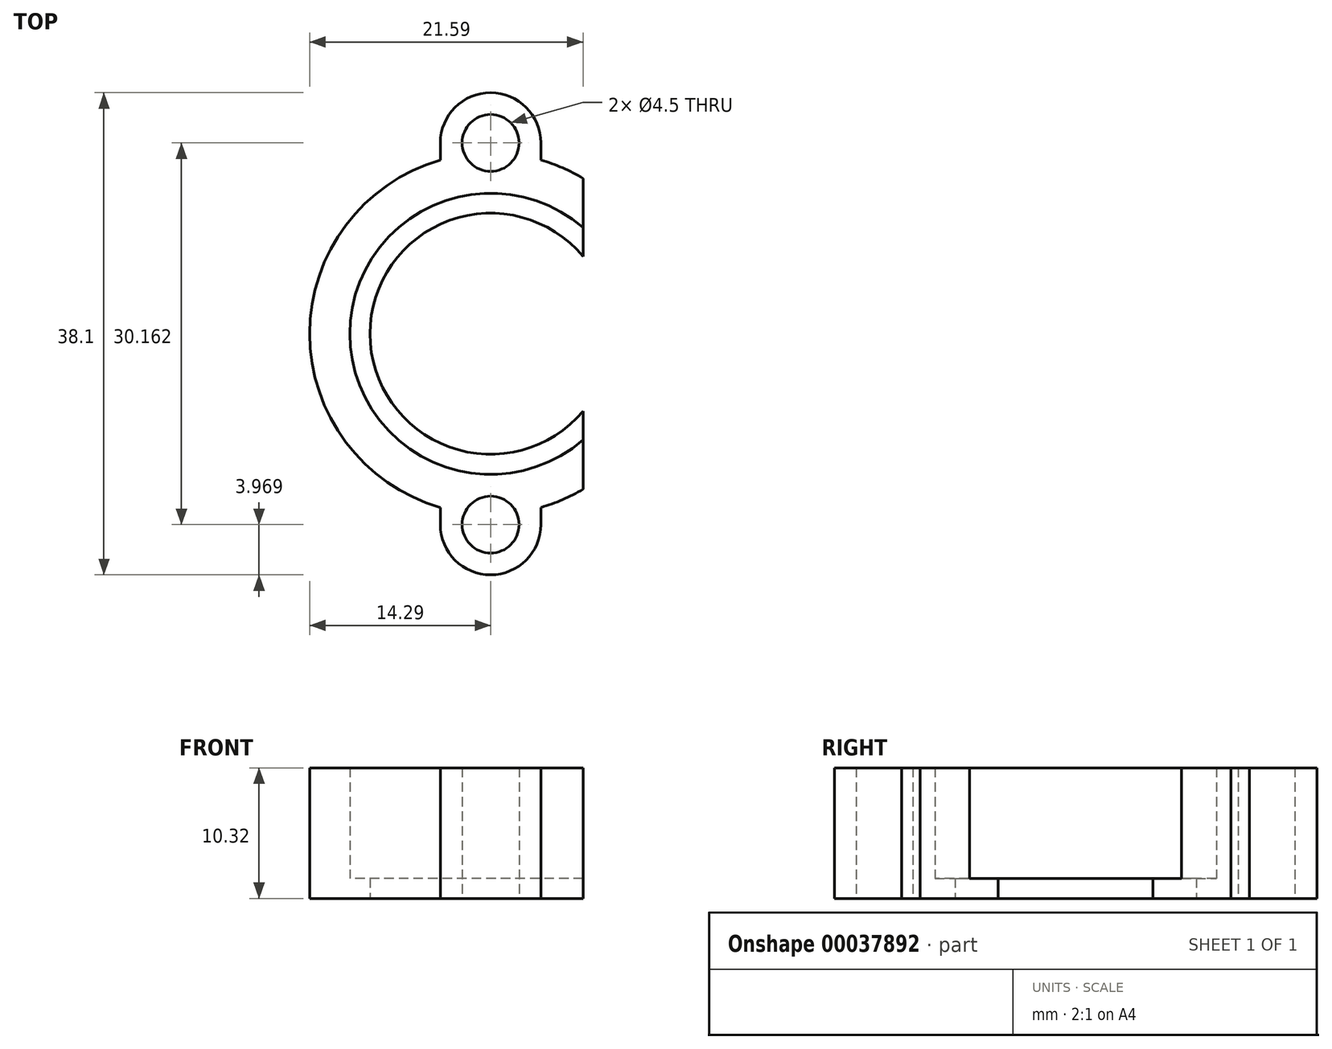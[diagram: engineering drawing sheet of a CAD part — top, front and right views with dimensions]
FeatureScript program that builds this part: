
annotation { "Feature Type Name" : "Feature", "Feature Type Description" : "" }
export const myFeature = defineFeature(function(context is Context, id is Id, definition is map)
    precondition{}
    {
        {
            var Q0;
            Q0=qCreatedBy(makeId("Top.planeOp"),FACE);
            var sketch = newSketch(context, id + "F0", { "sketchPlane" : qUnion([Q0])});
            skCircle(sketch, "E0", {"center": v(0, 0) * mm, "radius": 9.53 * mm});
            skArc(sketch, "E1", {"start": v(3.97, -13.73) * mm, "mid": v(14.29, 0) * mm, "end": v(3.97, 13.73) * mm});
            skArc(sketch, "E2", {"start": v(-3.97, 13.73) * mm, "mid": v(-14.29, 0) * mm, "end": v(-3.97, -13.73) * mm});
            skLineSegment(sketch, "E3", {"start": v(0, -15.08) * mm, "end": v(0, 15.08) * mm, "construction": true});
            skLineSegment(sketch, "E4", {"start": v(-3.97, 15.08) * mm, "end": v(3.97, 15.08) * mm, "construction": true});
            skLineSegment(sketch, "E5", {"start": v(-3.97, 15.08) * mm, "end": v(-3.97, 13.73) * mm});
            skLineSegment(sketch, "E6", {"start": v(3.97, 15.08) * mm, "end": v(3.97, 13.73) * mm});
            skLineSegment(sketch, "E7", {"start": v(-3.97, -15.08) * mm, "end": v(3.97, -15.08) * mm, "construction": true});
            skLineSegment(sketch, "E8", {"start": v(3.97, -15.08) * mm, "end": v(3.97, -13.73) * mm});
            skLineSegment(sketch, "E9", {"start": v(-3.97, -15.08) * mm, "end": v(-3.97, -13.73) * mm});
            skArc(sketch, "E10", {"start": v(3.97, 15.08) * mm, "mid": v(0, 19.05) * mm, "end": v(-3.97, 15.08) * mm});
            skArc(sketch, "E11", {"start": v(-3.97, -15.08) * mm, "mid": v(0, -19.05) * mm, "end": v(3.97, -15.08) * mm});
            skCircle(sketch, "E12", {"center": v(0, 15.08) * mm, "radius": 2.25 * mm});
            skCircle(sketch, "E13", {"center": v(0, -15.08) * mm, "radius": 2.25 * mm});
            skSolve(sketch);
        }
        {
            var Q0;
            Q0=qSketchRegion(id+"F0",true);
            extrude(context, id + "F1", {"entities" : qUnion([Q0]), "depth" : 1.59 * mm});
        }
        {
            var Q0;
            Q0=makeQuery(id+"F1.opExtrude","CAP_FACE",FACE,{"disambiguationData":[OSD([sQuery(id+"F0.wireOp",EDGE,"E0"),sQuery(id+"F0.wireOp",EDGE,"E1"),sQuery(id+"F0.wireOp",EDGE,"E2"),sQuery(id+"F0.wireOp",EDGE,"E5"),sQuery(id+"F0.wireOp",EDGE,"E6"),sQuery(id+"F0.wireOp",EDGE,"E8"),sQuery(id+"F0.wireOp",EDGE,"E9"),sQuery(id+"F0.wireOp",EDGE,"E10"),sQuery(id+"F0.wireOp",EDGE,"E11"),sQuery(id+"F0.wireOp",EDGE,"E12"),sQuery(id+"F0.wireOp",EDGE,"E13")])],"isStart":false});
            var sketch = newSketch(context, id + "F2", { "sketchPlane" : qUnion([Q0])});
            skCircle(sketch, "E14", {"center": v(0, 0) * mm, "radius": 11.11 * mm});
            skSolve(sketch);
        }
        {
            var Q0;
            Q0=makeQuery(id+"F2.imprint","IMPRINT",FACE,{"disambiguationData":[TD([[makeQuery(id+"F2.imprint","IMPRINT",EDGE,{"derivedFrom":sQuery(id+"F2.wireOp",EDGE,"E14")}),-1.0]])]});
            extrude(context, id + "F3", {"entities" : qUnion([Q0]), "operationType" : NewBodyOperationType.ADD, "depth" : 8.73 * mm});
        }
        {
            var Q0;
            Q0=makeQuery(id+"F3.opExtrude","CAP_FACE",FACE,{"disambiguationData":[OSD([sQuery(id+"F0.wireOp",EDGE,"E1"),sQuery(id+"F0.wireOp",EDGE,"E2"),sQuery(id+"F0.wireOp",EDGE,"E5"),sQuery(id+"F0.wireOp",EDGE,"E6"),sQuery(id+"F0.wireOp",EDGE,"E8"),sQuery(id+"F0.wireOp",EDGE,"E9"),sQuery(id+"F0.wireOp",EDGE,"E10"),sQuery(id+"F0.wireOp",EDGE,"E11"),sQuery(id+"F0.wireOp",EDGE,"E12"),sQuery(id+"F0.wireOp",EDGE,"E13"),sQuery(id+"F2.wireOp",EDGE,"E14")])],"isStart":false});
            var sketch = newSketch(context, id + "F4", { "sketchPlane" : qUnion([Q0])});
            skLineSegment(sketch, "E15", {"start": v(0, 0) * mm, "end": v(7.3, 0) * mm});
            skLineSegment(sketch, "E16.bottom", {"start": v(7.3, -14.29) * mm, "end": v(14.29, -14.29) * mm});
            skLineSegment(sketch, "E16.top", {"start": v(7.3, 14.29) * mm, "end": v(14.29, 14.29) * mm});
            skLineSegment(sketch, "E16.left", {"start": v(7.3, -14.29) * mm, "end": v(7.3, 14.29) * mm});
            skLineSegment(sketch, "E16.right", {"start": v(14.29, -14.29) * mm, "end": v(14.29, 14.29) * mm});
            skSolve(sketch);
        }
        {
            var Q0;
            Q0 = qSketchRegion(id + "F4", true);
            var Q1;
            Q1=makeQuery(id+"F1.opExtrude","CAP_FACE",FACE,{"disambiguationData":[OSD([sQuery(id+"F0.wireOp",EDGE,"E0"),sQuery(id+"F0.wireOp",EDGE,"E1"),sQuery(id+"F0.wireOp",EDGE,"E2"),sQuery(id+"F0.wireOp",EDGE,"E5"),sQuery(id+"F0.wireOp",EDGE,"E6"),sQuery(id+"F0.wireOp",EDGE,"E8"),sQuery(id+"F0.wireOp",EDGE,"E9"),sQuery(id+"F0.wireOp",EDGE,"E10"),sQuery(id+"F0.wireOp",EDGE,"E11"),sQuery(id+"F0.wireOp",EDGE,"E12"),sQuery(id+"F0.wireOp",EDGE,"E13")])],"isStart":true});
            extrude(context, id + "F5", {"entities" : qUnion([Q0]), "operationType" : NewBodyOperationType.REMOVE, "endBound" : BoundingType.UP_TO_SURFACE, "oppositeDirection" : true, "endBoundEntityFace" : qUnion([Q1]), "depth" : 25.4 * mm});
        }
    });
